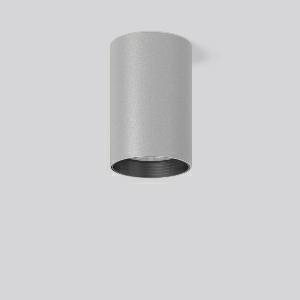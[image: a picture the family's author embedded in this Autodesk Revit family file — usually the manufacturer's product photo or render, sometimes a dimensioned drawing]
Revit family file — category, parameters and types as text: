
# Revit family: heledon_maxi_a_931221_004_2_2a55
name_source: partatom
category: Lighting Fixtures
units: mm (PartAtom-declared; Revit-internal decimal feet)

## family parameters
Cut with Voids When Loaded = No
Host = Face
Light Source = No
Part Type = Normal
Room Calculation Point = No
Round Connector Dimension = Use Diameter
Shared = No

## types (1)
- HELEDON maxi A (1 x LED Modul 927, 2550 lm, 2700)
    Apparent Load = 25 VA
    Approval mark = CE
    CIE Flux Codes = 96 100 100 100 100
    Color Rendering = 92
    Color Temperature = 2700
    Default Elevation = 1800 mm
    Description = Series: HELEDON maxi
Cylindrical surface-mounted downlight. Housing: die-cast aluminium, powder-coated. Internal ceiling frame polycarbonate with bayonet mounting. Black plastic ring and recessed LED to prevent glare from the side. Optical assembly with lens made of plastic (polycarbonate) for the best homogeneous light distribution - can be changed without tools. Best colour rendering index Ra>90. Suitable for Ceiling mounting. Easy installation with a separate ceiling frame with bayonet mounting and plug connection. Driver integrated. Connected via plug-in connector. High quality converter without flickering and stroboscopic effect. The following accessories can be mounted without use of tools: interchangeable lenses, decorative glasses, honeycomb louvre, clear and frosted diffusers, white interchangeable plastic ring. 
Colour: silver
Diameter: 123 mm
Height: 183 mm
Lamp: LED
Socket: without socket
Colour temperature: 2700K
Colour rendering index (CRI): 92
System power: 25 W
Rated luminous flux: 2550 lm
Luminous efficiency: 102 lm/W
Control gear: Regulated power supply
Protection class: I
Type of protection: IP 20
    Height = 183 mm
    Lamp = 1 x LED Modul 927
    Lamp Light Flux = 2550 lm
    Lamp count = 1
    Length = 123 mm
    Lifetime = 50000 h
    Luminous efficacy = 102 lm/W
    Manufacturer = RZB
    ModVariant = No
    Model = 931221.004.2
    Mounting Place = Ceiling
    Mounting Type = Surface mounted
    Number of Poles = 1
    OnlyDefault = Yes
    Power Factor = 1
    Product Name = HELEDON maxi A
    Product group = Surface mounted downlights
    ProductGroupID = 302
    Protection Class = Protection class I
    Protection Degree = IP 20
    RLX_Detail_Level = 1
    RLX_Emergency_Light_Flux = 0 lm
    RLX_Emergency_Type = 0
    RLX_Emergency_Type_DB = No
    RlxData = <blob elided: 99061 chars, md5=b0aa62f4>
    Socket = socket
    Standby Power = 0 W
    System Light Flux = 2550 lm
    System Power = 25 W
    Type Comments = Product without accessories
    Type Image = 931193.004.jpg
    URL = http://relux.com
    VarID = ---
    Voltage = 230 V
    Voltage Range = 220-240 V
    Weight = 0.00 kg
    Width = 0 mm  [stored 0 ft]

note: [stored X ft] marks values corroborated as IEEE doubles in the binary element streams (Revit-internal decimal feet)

## geometry (parser evidence)
native form markers: Blend x4, Sweep x11
no freeform markers — native parametric forms only
